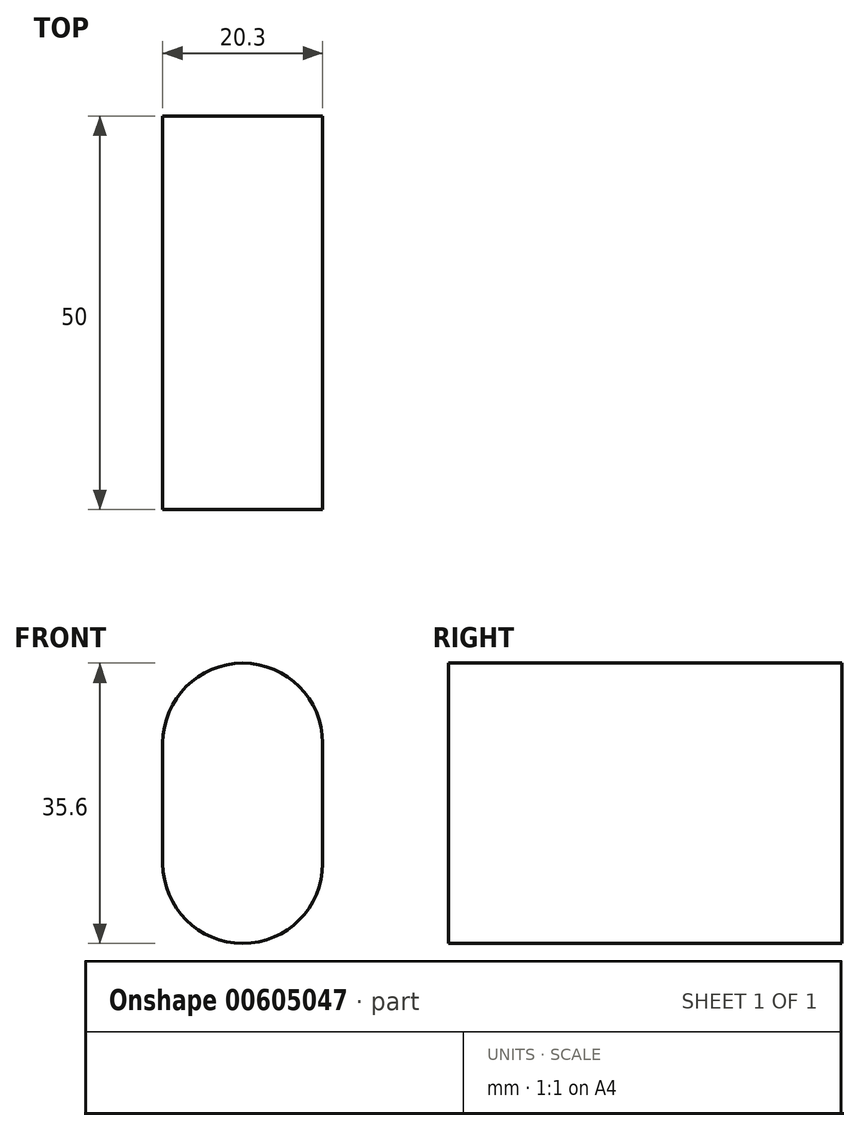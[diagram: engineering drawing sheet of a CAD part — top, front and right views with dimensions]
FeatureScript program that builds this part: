
annotation { "Feature Type Name" : "Feature", "Feature Type Description" : "" }
export const myFeature = defineFeature(function(context is Context, id is Id, definition is map)
    precondition{}
    {
        {
            var Q0;
            Q0=qCreatedBy(makeId("Front.planeOp"),FACE);
            var sketch = newSketch(context, id + "F0", { "sketchPlane" : qUnion([Q0])});
            skLineSegment(sketch, "E0", {"start": v(-10.15, 7.65) * mm, "end": v(-10.15, -7.65) * mm});
            skArc(sketch, "E1", {"start": v(-10.15, -7.65) * mm, "mid": v(0, -17.8) * mm, "end": v(10.15, -7.65) * mm});
            skArc(sketch, "E2", {"start": v(10.15, 7.65) * mm, "mid": v(0, 17.8) * mm, "end": v(-10.15, 7.65) * mm});
            skLineSegment(sketch, "E3", {"start": v(10.15, 7.65) * mm, "end": v(10.15, -7.65) * mm});
            skPoint(sketch, "E4", {"position": v(0, 0) * mm});
            skPoint(sketch, "E4.positionSnap0", {"position": v(-10.15, 0) * mm});
            skSolve(sketch);
        }
        {
            var Q0;
            Q0=makeQuery(id+"F0.imprint","IMPRINT",FACE,{"disambiguationData":[TD([[makeQuery(id+"F0.imprint","IMPRINT",EDGE,{"derivedFrom":sQuery(id+"F0.wireOp",EDGE,"E0")}),1.0]])]});
            extrude(context, id + "F1", {"entities" : qUnion([Q0]), "oppositeDirection" : true, "depth" : 50 * mm, "offsetDistance" : 25 * mm});
        }
    });
